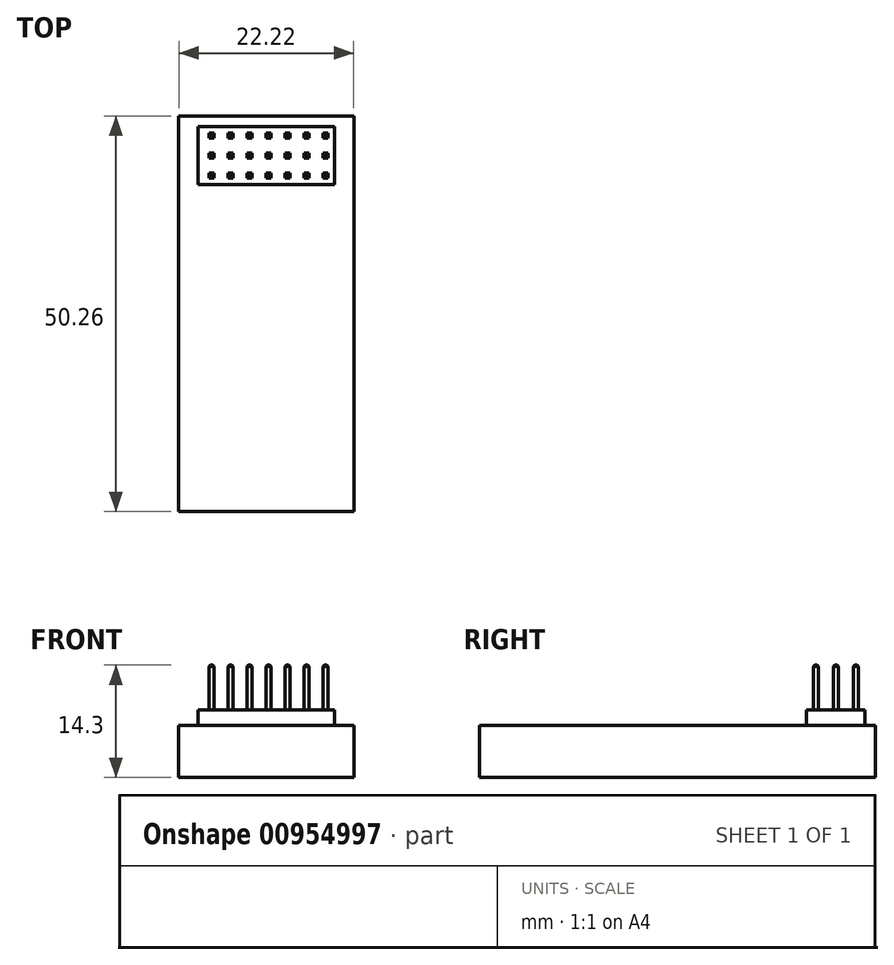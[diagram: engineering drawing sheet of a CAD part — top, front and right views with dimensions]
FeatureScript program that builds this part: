
annotation { "Feature Type Name" : "Feature", "Feature Type Description" : "" }
export const myFeature = defineFeature(function(context is Context, id is Id, definition is map)
    precondition{}
    {
        {
            var Q0;
            Q0=qCreatedBy(makeId("Top.planeOp"),FACE);
            var sketch = newSketch(context, id + "F0", { "sketchPlane" : qUnion([Q0])});
            skLineSegment(sketch, "E0.bottom", {"start": v(11.11, 25.13) * mm, "end": v(-11.11, 25.13) * mm});
            skLineSegment(sketch, "E0.top", {"start": v(11.11, -25.13) * mm, "end": v(-11.11, -25.13) * mm});
            skLineSegment(sketch, "E0.left", {"start": v(11.11, 25.13) * mm, "end": v(11.11, -25.13) * mm});
            skLineSegment(sketch, "E0.right", {"start": v(-11.11, 25.13) * mm, "end": v(-11.11, -25.13) * mm});
            skPoint(sketch, "E0.middle", {"position": v(0, 0) * mm});
            skSolve(sketch);
        }
        {
            var Q0;
            Q0 = qSketchRegion(id + "F0", true);
            extrude(context, id + "F1", {"entities" : qUnion([Q0]), "depth" : 6.63 * mm, "offsetDistance" : 25.4 * mm});
        }
        {
            var Q0;
            Q0=makeQuery(id+"F1.opExtrude","CAP_FACE",FACE,{"disambiguationData":[OSD([sQuery(id+"F0.wireOp",EDGE,"E0.bottom"),sQuery(id+"F0.wireOp",EDGE,"E0.top"),sQuery(id+"F0.wireOp",EDGE,"E0.left"),sQuery(id+"F0.wireOp",EDGE,"E0.right")])],"isStart":false});
            var sketch = newSketch(context, id + "F2", { "sketchPlane" : qUnion([Q0])});
            skLineSegment(sketch, "E1.bottom", {"start": v(-8.68, 23.79) * mm, "end": v(8.68, 23.79) * mm});
            skLineSegment(sketch, "E1.top", {"start": v(-8.68, 16.38) * mm, "end": v(8.68, 16.38) * mm});
            skLineSegment(sketch, "E1.left", {"start": v(-8.68, 23.79) * mm, "end": v(-8.68, 16.38) * mm});
            skLineSegment(sketch, "E1.right", {"start": v(8.68, 23.79) * mm, "end": v(8.68, 16.38) * mm});
            skPoint(sketch, "E2", {"position": v(0, 16.38) * mm});
            skSolve(sketch);
        }
        {
            var Q0;
            Q0 = qSketchRegion(id + "F2", true);
            extrude(context, id + "F3", {"entities" : qUnion([Q0]), "operationType" : NewBodyOperationType.ADD, "depth" : 1.96 * mm, "offsetDistance" : 25.4 * mm});
        }
        {
            var Q0;
            Q0=makeQuery(id+"F3.opExtrude","CAP_FACE",FACE,{"disambiguationData":[OSD([sQuery(id+"F2.wireOp",EDGE,"E1.bottom"),sQuery(id+"F2.wireOp",EDGE,"E1.top"),sQuery(id+"F2.wireOp",EDGE,"E1.left"),sQuery(id+"F2.wireOp",EDGE,"E1.right")])],"isStart":false});
            var sketch = newSketch(context, id + "F4", { "sketchPlane" : qUnion([Q0])});
            skLineSegment(sketch, "E3.bottom", {"start": v(7.2, 22.96) * mm, "end": v(7.83, 22.96) * mm});
            skLineSegment(sketch, "E3.top", {"start": v(7.2, 22.33) * mm, "end": v(7.83, 22.33) * mm});
            skLineSegment(sketch, "E3.left", {"start": v(7.2, 22.96) * mm, "end": v(7.2, 22.33) * mm});
            skLineSegment(sketch, "E3.right", {"start": v(7.83, 22.96) * mm, "end": v(7.83, 22.33) * mm});
            skLineSegment(sketch, "E4.1.0.0", {"start": v(4.78, 22.96) * mm, "end": v(5.42, 22.96) * mm});
            skLineSegment(sketch, "E4.1.0.1", {"start": v(4.78, 22.96) * mm, "end": v(4.78, 22.33) * mm});
            skLineSegment(sketch, "E4.1.0.2", {"start": v(4.78, 22.33) * mm, "end": v(5.42, 22.33) * mm});
            skLineSegment(sketch, "E4.1.0.3", {"start": v(5.42, 22.96) * mm, "end": v(5.42, 22.33) * mm});
            skLineSegment(sketch, "E4.2.0.0", {"start": v(2.37, 22.96) * mm, "end": v(3, 22.96) * mm});
            skLineSegment(sketch, "E4.2.0.1", {"start": v(2.37, 22.96) * mm, "end": v(2.37, 22.33) * mm});
            skLineSegment(sketch, "E4.2.0.2", {"start": v(2.37, 22.33) * mm, "end": v(3, 22.33) * mm});
            skLineSegment(sketch, "E4.2.0.3", {"start": v(3, 22.96) * mm, "end": v(3, 22.33) * mm});
            skLineSegment(sketch, "E4.3.0.0", {"start": v(-0.04, 22.96) * mm, "end": v(0.6, 22.96) * mm});
            skLineSegment(sketch, "E4.3.0.1", {"start": v(-0.04, 22.96) * mm, "end": v(-0.04, 22.33) * mm});
            skLineSegment(sketch, "E4.3.0.2", {"start": v(-0.04, 22.33) * mm, "end": v(0.6, 22.33) * mm});
            skLineSegment(sketch, "E4.3.0.3", {"start": v(0.6, 22.96) * mm, "end": v(0.6, 22.33) * mm});
            skLineSegment(sketch, "E4.4.0.0", {"start": v(-2.46, 22.96) * mm, "end": v(-1.82, 22.96) * mm});
            skLineSegment(sketch, "E4.4.0.1", {"start": v(-2.46, 22.96) * mm, "end": v(-2.46, 22.33) * mm});
            skLineSegment(sketch, "E4.4.0.2", {"start": v(-2.46, 22.33) * mm, "end": v(-1.82, 22.33) * mm});
            skLineSegment(sketch, "E4.4.0.3", {"start": v(-1.82, 22.96) * mm, "end": v(-1.82, 22.33) * mm});
            skLineSegment(sketch, "E4.5.0.0", {"start": v(-4.87, 22.96) * mm, "end": v(-4.24, 22.96) * mm});
            skLineSegment(sketch, "E4.5.0.1", {"start": v(-4.87, 22.96) * mm, "end": v(-4.87, 22.33) * mm});
            skLineSegment(sketch, "E4.5.0.2", {"start": v(-4.87, 22.33) * mm, "end": v(-4.24, 22.33) * mm});
            skLineSegment(sketch, "E4.5.0.3", {"start": v(-4.24, 22.96) * mm, "end": v(-4.24, 22.33) * mm});
            skLineSegment(sketch, "E4.6.0.0", {"start": v(-7.28, 22.96) * mm, "end": v(-6.65, 22.96) * mm});
            skLineSegment(sketch, "E4.6.0.1", {"start": v(-7.28, 22.96) * mm, "end": v(-7.28, 22.33) * mm});
            skLineSegment(sketch, "E4.6.0.2", {"start": v(-7.28, 22.33) * mm, "end": v(-6.65, 22.33) * mm});
            skLineSegment(sketch, "E4.6.0.3", {"start": v(-6.65, 22.96) * mm, "end": v(-6.65, 22.33) * mm});
            skLineSegment(sketch, "E4.direction1", {"start": v(7.2, 22.96) * mm, "end": v(4.78, 22.96) * mm, "construction": true});
            skLineSegment(sketch, "E5.1.0.0", {"start": v(-6.65, 20.42) * mm, "end": v(-6.65, 19.79) * mm});
            skLineSegment(sketch, "E5.1.0.1", {"start": v(-7.28, 20.42) * mm, "end": v(-6.65, 20.42) * mm});
            skLineSegment(sketch, "E5.1.0.2", {"start": v(-7.28, 20.42) * mm, "end": v(-7.28, 19.79) * mm});
            skLineSegment(sketch, "E5.1.0.3", {"start": v(-7.28, 19.79) * mm, "end": v(-6.65, 19.79) * mm});
            skLineSegment(sketch, "E5.1.0.4", {"start": v(-4.87, 20.42) * mm, "end": v(-4.87, 19.79) * mm});
            skLineSegment(sketch, "E5.1.0.5", {"start": v(-4.87, 20.42) * mm, "end": v(-4.24, 20.42) * mm});
            skLineSegment(sketch, "E5.1.0.6", {"start": v(-4.87, 19.79) * mm, "end": v(-4.24, 19.79) * mm});
            skLineSegment(sketch, "E5.1.0.7", {"start": v(-4.24, 20.42) * mm, "end": v(-4.24, 19.79) * mm});
            skLineSegment(sketch, "E5.1.0.8", {"start": v(-2.46, 20.42) * mm, "end": v(-2.46, 19.79) * mm});
            skLineSegment(sketch, "E5.1.0.9", {"start": v(-2.46, 20.42) * mm, "end": v(-1.82, 20.42) * mm});
            skLineSegment(sketch, "E5.1.0.10", {"start": v(-2.46, 19.79) * mm, "end": v(-1.82, 19.79) * mm});
            skLineSegment(sketch, "E5.1.0.11", {"start": v(-1.82, 20.42) * mm, "end": v(-1.82, 19.79) * mm});
            skLineSegment(sketch, "E5.1.0.12", {"start": v(-0.04, 20.42) * mm, "end": v(-0.04, 19.79) * mm});
            skLineSegment(sketch, "E5.1.0.13", {"start": v(-0.04, 20.42) * mm, "end": v(0.6, 20.42) * mm});
            skLineSegment(sketch, "E5.1.0.14", {"start": v(0.6, 20.42) * mm, "end": v(0.6, 19.79) * mm});
            skLineSegment(sketch, "E5.1.0.15", {"start": v(-0.04, 19.79) * mm, "end": v(0.6, 19.79) * mm});
            skLineSegment(sketch, "E5.1.0.16", {"start": v(2.37, 20.42) * mm, "end": v(2.37, 19.79) * mm});
            skLineSegment(sketch, "E5.1.0.17", {"start": v(2.37, 19.79) * mm, "end": v(3, 19.79) * mm});
            skLineSegment(sketch, "E5.1.0.18", {"start": v(2.37, 20.42) * mm, "end": v(3, 20.42) * mm});
            skLineSegment(sketch, "E5.1.0.19", {"start": v(3, 20.42) * mm, "end": v(3, 19.79) * mm});
            skLineSegment(sketch, "E5.1.0.20", {"start": v(4.78, 20.42) * mm, "end": v(4.78, 19.79) * mm});
            skLineSegment(sketch, "E5.1.0.21", {"start": v(5.42, 20.42) * mm, "end": v(5.42, 19.79) * mm});
            skLineSegment(sketch, "E5.1.0.22", {"start": v(4.78, 19.79) * mm, "end": v(5.42, 19.79) * mm});
            skLineSegment(sketch, "E5.1.0.23", {"start": v(7.2, 19.79) * mm, "end": v(7.83, 19.79) * mm});
            skLineSegment(sketch, "E5.1.0.24", {"start": v(7.83, 20.42) * mm, "end": v(7.83, 19.79) * mm});
            skLineSegment(sketch, "E5.1.0.25", {"start": v(7.2, 20.42) * mm, "end": v(7.2, 19.79) * mm});
            skLineSegment(sketch, "E5.1.0.26", {"start": v(7.2, 20.42) * mm, "end": v(7.83, 20.42) * mm});
            skLineSegment(sketch, "E5.2.0.0", {"start": v(-6.65, 17.88) * mm, "end": v(-6.65, 17.25) * mm});
            skLineSegment(sketch, "E5.2.0.1", {"start": v(-7.28, 17.88) * mm, "end": v(-6.65, 17.88) * mm});
            skLineSegment(sketch, "E5.2.0.2", {"start": v(-7.28, 17.88) * mm, "end": v(-7.28, 17.25) * mm});
            skLineSegment(sketch, "E5.2.0.3", {"start": v(-7.28, 17.25) * mm, "end": v(-6.65, 17.25) * mm});
            skLineSegment(sketch, "E5.2.0.4", {"start": v(-4.87, 17.88) * mm, "end": v(-4.87, 17.25) * mm});
            skLineSegment(sketch, "E5.2.0.5", {"start": v(-4.87, 17.88) * mm, "end": v(-4.24, 17.88) * mm});
            skLineSegment(sketch, "E5.2.0.6", {"start": v(-4.87, 17.25) * mm, "end": v(-4.24, 17.25) * mm});
            skLineSegment(sketch, "E5.2.0.7", {"start": v(-4.24, 17.88) * mm, "end": v(-4.24, 17.25) * mm});
            skLineSegment(sketch, "E5.2.0.8", {"start": v(-2.46, 17.88) * mm, "end": v(-2.46, 17.25) * mm});
            skLineSegment(sketch, "E5.2.0.9", {"start": v(-2.46, 17.88) * mm, "end": v(-1.82, 17.88) * mm});
            skLineSegment(sketch, "E5.2.0.10", {"start": v(-2.46, 17.25) * mm, "end": v(-1.82, 17.25) * mm});
            skLineSegment(sketch, "E5.2.0.11", {"start": v(-1.82, 17.88) * mm, "end": v(-1.82, 17.25) * mm});
            skLineSegment(sketch, "E5.2.0.12", {"start": v(-0.04, 17.88) * mm, "end": v(-0.04, 17.25) * mm});
            skLineSegment(sketch, "E5.2.0.13", {"start": v(-0.04, 17.88) * mm, "end": v(0.6, 17.88) * mm});
            skLineSegment(sketch, "E5.2.0.14", {"start": v(0.6, 17.88) * mm, "end": v(0.6, 17.25) * mm});
            skLineSegment(sketch, "E5.2.0.15", {"start": v(-0.04, 17.25) * mm, "end": v(0.6, 17.25) * mm});
            skLineSegment(sketch, "E5.2.0.16", {"start": v(2.37, 17.88) * mm, "end": v(2.37, 17.25) * mm});
            skLineSegment(sketch, "E5.2.0.17", {"start": v(2.37, 17.25) * mm, "end": v(3, 17.25) * mm});
            skLineSegment(sketch, "E5.2.0.18", {"start": v(2.37, 17.88) * mm, "end": v(3, 17.88) * mm});
            skLineSegment(sketch, "E5.2.0.19", {"start": v(3, 17.88) * mm, "end": v(3, 17.25) * mm});
            skLineSegment(sketch, "E5.2.0.20", {"start": v(4.78, 17.88) * mm, "end": v(4.78, 17.25) * mm});
            skLineSegment(sketch, "E5.2.0.21", {"start": v(5.42, 17.88) * mm, "end": v(5.42, 17.25) * mm});
            skLineSegment(sketch, "E5.2.0.22", {"start": v(4.78, 17.25) * mm, "end": v(5.42, 17.25) * mm});
            skLineSegment(sketch, "E5.2.0.23", {"start": v(7.2, 17.25) * mm, "end": v(7.83, 17.25) * mm});
            skLineSegment(sketch, "E5.2.0.24", {"start": v(7.83, 17.88) * mm, "end": v(7.83, 17.25) * mm});
            skLineSegment(sketch, "E5.2.0.25", {"start": v(7.2, 17.88) * mm, "end": v(7.2, 17.25) * mm});
            skLineSegment(sketch, "E5.2.0.26", {"start": v(7.2, 17.88) * mm, "end": v(7.83, 17.88) * mm});
            skLineSegment(sketch, "E5.direction1", {"start": v(-6.65, 22.33) * mm, "end": v(-6.65, 19.79) * mm, "construction": true});
            skLineSegment(sketch, "E6", {"start": v(4.78, 20.42) * mm, "end": v(5.42, 20.42) * mm});
            skLineSegment(sketch, "E7", {"start": v(4.78, 17.88) * mm, "end": v(5.42, 17.88) * mm});
            skSolve(sketch);
        }
        {
            var Q0;
            Q0 = qSketchRegion(id + "F4", true);
            extrude(context, id + "F5", {"entities" : qUnion([Q0]), "operationType" : NewBodyOperationType.ADD, "depth" : 5.7 * mm, "offsetDistance" : 25.4 * mm});
        }
        {
            var Q0;
            Q0=makeQuery(id+"F5.opExtrude","CAP_FACE",FACE,{"disambiguationData":[OSD([sQuery(id+"F4.wireOp",EDGE,"E4.6.0.0"),sQuery(id+"F4.wireOp",EDGE,"E4.6.0.1"),sQuery(id+"F4.wireOp",EDGE,"E4.6.0.2"),sQuery(id+"F4.wireOp",EDGE,"E4.6.0.3")])],"isStart":false});
            var Q1;
            Q1=makeQuery(id+"F5.opExtrude","CAP_FACE",FACE,{"disambiguationData":[OSD([sQuery(id+"F4.wireOp",EDGE,"E5.1.0.0"),sQuery(id+"F4.wireOp",EDGE,"E5.1.0.1"),sQuery(id+"F4.wireOp",EDGE,"E5.1.0.2"),sQuery(id+"F4.wireOp",EDGE,"E5.1.0.3")])],"isStart":false});
            var Q2;
            Q2=makeQuery(id+"F5.opExtrude","CAP_FACE",FACE,{"disambiguationData":[OSD([sQuery(id+"F4.wireOp",EDGE,"E4.5.0.0"),sQuery(id+"F4.wireOp",EDGE,"E4.5.0.1"),sQuery(id+"F4.wireOp",EDGE,"E4.5.0.2"),sQuery(id+"F4.wireOp",EDGE,"E4.5.0.3")])],"isStart":false});
            var Q3;
            Q3=makeQuery(id+"F5.opExtrude","CAP_FACE",FACE,{"disambiguationData":[OSD([sQuery(id+"F4.wireOp",EDGE,"E5.1.0.4"),sQuery(id+"F4.wireOp",EDGE,"E5.1.0.5"),sQuery(id+"F4.wireOp",EDGE,"E5.1.0.6"),sQuery(id+"F4.wireOp",EDGE,"E5.1.0.7")])],"isStart":false});
            var Q4;
            Q4=makeQuery(id+"F5.opExtrude","CAP_FACE",FACE,{"disambiguationData":[OSD([sQuery(id+"F4.wireOp",EDGE,"E5.2.0.0"),sQuery(id+"F4.wireOp",EDGE,"E5.2.0.1"),sQuery(id+"F4.wireOp",EDGE,"E5.2.0.2"),sQuery(id+"F4.wireOp",EDGE,"E5.2.0.3")])],"isStart":false});
            var Q5;
            Q5=makeQuery(id+"F5.opExtrude","CAP_FACE",FACE,{"disambiguationData":[OSD([sQuery(id+"F4.wireOp",EDGE,"E5.2.0.4"),sQuery(id+"F4.wireOp",EDGE,"E5.2.0.5"),sQuery(id+"F4.wireOp",EDGE,"E5.2.0.6"),sQuery(id+"F4.wireOp",EDGE,"E5.2.0.7")])],"isStart":false});
            var Q6;
            Q6=makeQuery(id+"F5.opExtrude","CAP_FACE",FACE,{"disambiguationData":[OSD([sQuery(id+"F4.wireOp",EDGE,"E5.1.0.8"),sQuery(id+"F4.wireOp",EDGE,"E5.1.0.9"),sQuery(id+"F4.wireOp",EDGE,"E5.1.0.10"),sQuery(id+"F4.wireOp",EDGE,"E5.1.0.11")])],"isStart":false});
            var Q7;
            Q7=makeQuery(id+"F5.opExtrude","CAP_EDGE",EDGE,{"disambiguationData":[OSD([sQuery(id+"F4.wireOp",EDGE,"E4.4.0.0")])],"isStart":false});
            var Q8;
            Q8=makeQuery(id+"F5.opExtrude","CAP_FACE",FACE,{"disambiguationData":[OSD([sQuery(id+"F4.wireOp",EDGE,"E4.4.0.0"),sQuery(id+"F4.wireOp",EDGE,"E4.4.0.1"),sQuery(id+"F4.wireOp",EDGE,"E4.4.0.2"),sQuery(id+"F4.wireOp",EDGE,"E4.4.0.3")])],"isStart":false});
            var Q9;
            Q9=makeQuery(id+"F5.opExtrude","CAP_FACE",FACE,{"disambiguationData":[OSD([sQuery(id+"F4.wireOp",EDGE,"E5.2.0.8"),sQuery(id+"F4.wireOp",EDGE,"E5.2.0.9"),sQuery(id+"F4.wireOp",EDGE,"E5.2.0.10"),sQuery(id+"F4.wireOp",EDGE,"E5.2.0.11")])],"isStart":false});
            var Q10;
            Q10=makeQuery(id+"F5.opExtrude","CAP_FACE",FACE,{"disambiguationData":[OSD([sQuery(id+"F4.wireOp",EDGE,"E5.2.0.12"),sQuery(id+"F4.wireOp",EDGE,"E5.2.0.13"),sQuery(id+"F4.wireOp",EDGE,"E5.2.0.14"),sQuery(id+"F4.wireOp",EDGE,"E5.2.0.15")])],"isStart":false});
            var Q11;
            Q11=makeQuery(id+"F5.opExtrude","CAP_FACE",FACE,{"disambiguationData":[OSD([sQuery(id+"F4.wireOp",EDGE,"E5.1.0.12"),sQuery(id+"F4.wireOp",EDGE,"E5.1.0.13"),sQuery(id+"F4.wireOp",EDGE,"E5.1.0.14"),sQuery(id+"F4.wireOp",EDGE,"E5.1.0.15")])],"isStart":false});
            var Q12;
            Q12=makeQuery(id+"F5.opExtrude","CAP_FACE",FACE,{"disambiguationData":[OSD([sQuery(id+"F4.wireOp",EDGE,"E4.3.0.0"),sQuery(id+"F4.wireOp",EDGE,"E4.3.0.1"),sQuery(id+"F4.wireOp",EDGE,"E4.3.0.2"),sQuery(id+"F4.wireOp",EDGE,"E4.3.0.3")])],"isStart":false});
            var Q13;
            Q13=makeQuery(id+"F5.opExtrude","CAP_FACE",FACE,{"disambiguationData":[OSD([sQuery(id+"F4.wireOp",EDGE,"E4.2.0.0"),sQuery(id+"F4.wireOp",EDGE,"E4.2.0.1"),sQuery(id+"F4.wireOp",EDGE,"E4.2.0.2"),sQuery(id+"F4.wireOp",EDGE,"E4.2.0.3")])],"isStart":false});
            var Q14;
            Q14=makeQuery(id+"F5.opExtrude","CAP_EDGE",EDGE,{"disambiguationData":[OSD([sQuery(id+"F4.wireOp",EDGE,"E5.1.0.16")])],"isStart":false});
            var Q15;
            Q15=makeQuery(id+"F5.opExtrude","CAP_EDGE",EDGE,{"disambiguationData":[OSD([sQuery(id+"F4.wireOp",EDGE,"E5.1.0.17")])],"isStart":false});
            var Q16;
            Q16=makeQuery(id+"F5.opExtrude","CAP_FACE",FACE,{"disambiguationData":[OSD([sQuery(id+"F4.wireOp",EDGE,"E5.1.0.16"),sQuery(id+"F4.wireOp",EDGE,"E5.1.0.17"),sQuery(id+"F4.wireOp",EDGE,"E5.1.0.18"),sQuery(id+"F4.wireOp",EDGE,"E5.1.0.19")])],"isStart":false});
            var Q17;
            Q17=makeQuery(id+"F5.opExtrude","CAP_FACE",FACE,{"disambiguationData":[OSD([sQuery(id+"F4.wireOp",EDGE,"E5.2.0.16"),sQuery(id+"F4.wireOp",EDGE,"E5.2.0.17"),sQuery(id+"F4.wireOp",EDGE,"E5.2.0.18"),sQuery(id+"F4.wireOp",EDGE,"E5.2.0.19")])],"isStart":false});
            var Q18;
            Q18=makeQuery(id+"F5.opExtrude","CAP_FACE",FACE,{"disambiguationData":[OSD([sQuery(id+"F4.wireOp",EDGE,"E5.1.0.20"),sQuery(id+"F4.wireOp",EDGE,"E5.1.0.21"),sQuery(id+"F4.wireOp",EDGE,"E5.1.0.22"),sQuery(id+"F4.wireOp",EDGE,"E6")])],"isStart":false});
            var Q19;
            Q19=makeQuery(id+"F5.opExtrude","CAP_FACE",FACE,{"disambiguationData":[OSD([sQuery(id+"F4.wireOp",EDGE,"E5.2.0.20"),sQuery(id+"F4.wireOp",EDGE,"E5.2.0.21"),sQuery(id+"F4.wireOp",EDGE,"E5.2.0.22"),sQuery(id+"F4.wireOp",EDGE,"E7")])],"isStart":false});
            var Q20;
            Q20=makeQuery(id+"F5.opExtrude","CAP_FACE",FACE,{"disambiguationData":[OSD([sQuery(id+"F4.wireOp",EDGE,"E4.1.0.0"),sQuery(id+"F4.wireOp",EDGE,"E4.1.0.1"),sQuery(id+"F4.wireOp",EDGE,"E4.1.0.2"),sQuery(id+"F4.wireOp",EDGE,"E4.1.0.3")])],"isStart":false});
            var Q21;
            Q21=makeQuery(id+"F5.opExtrude","CAP_FACE",FACE,{"disambiguationData":[OSD([sQuery(id+"F4.wireOp",EDGE,"E5.1.0.23"),sQuery(id+"F4.wireOp",EDGE,"E5.1.0.24"),sQuery(id+"F4.wireOp",EDGE,"E5.1.0.25"),sQuery(id+"F4.wireOp",EDGE,"E5.1.0.26")])],"isStart":false});
            var Q22;
            Q22=makeQuery(id+"F5.opExtrude","CAP_FACE",FACE,{"disambiguationData":[OSD([sQuery(id+"F4.wireOp",EDGE,"E5.2.0.23"),sQuery(id+"F4.wireOp",EDGE,"E5.2.0.24"),sQuery(id+"F4.wireOp",EDGE,"E5.2.0.25"),sQuery(id+"F4.wireOp",EDGE,"E5.2.0.26")])],"isStart":false});
            var Q23;
            Q23=makeQuery(id+"F5.opExtrude","CAP_FACE",FACE,{"disambiguationData":[OSD([sQuery(id+"F4.wireOp",EDGE,"E3.bottom"),sQuery(id+"F4.wireOp",EDGE,"E3.top"),sQuery(id+"F4.wireOp",EDGE,"E3.left"),sQuery(id+"F4.wireOp",EDGE,"E3.right")])],"isStart":false});
            chamfer(context, id + "F6", {"entities" : qUnion([Q0, Q1, Q2, Q3, Q4, Q5, Q6, Q7, Q8, Q9, Q10, Q11, Q12, Q13, Q14, Q15, Q16, Q17, Q18, Q19, Q20, Q21, Q22, Q23]), "width" : 0.18 * mm, "tangentPropagation" : true});
        }
    });
